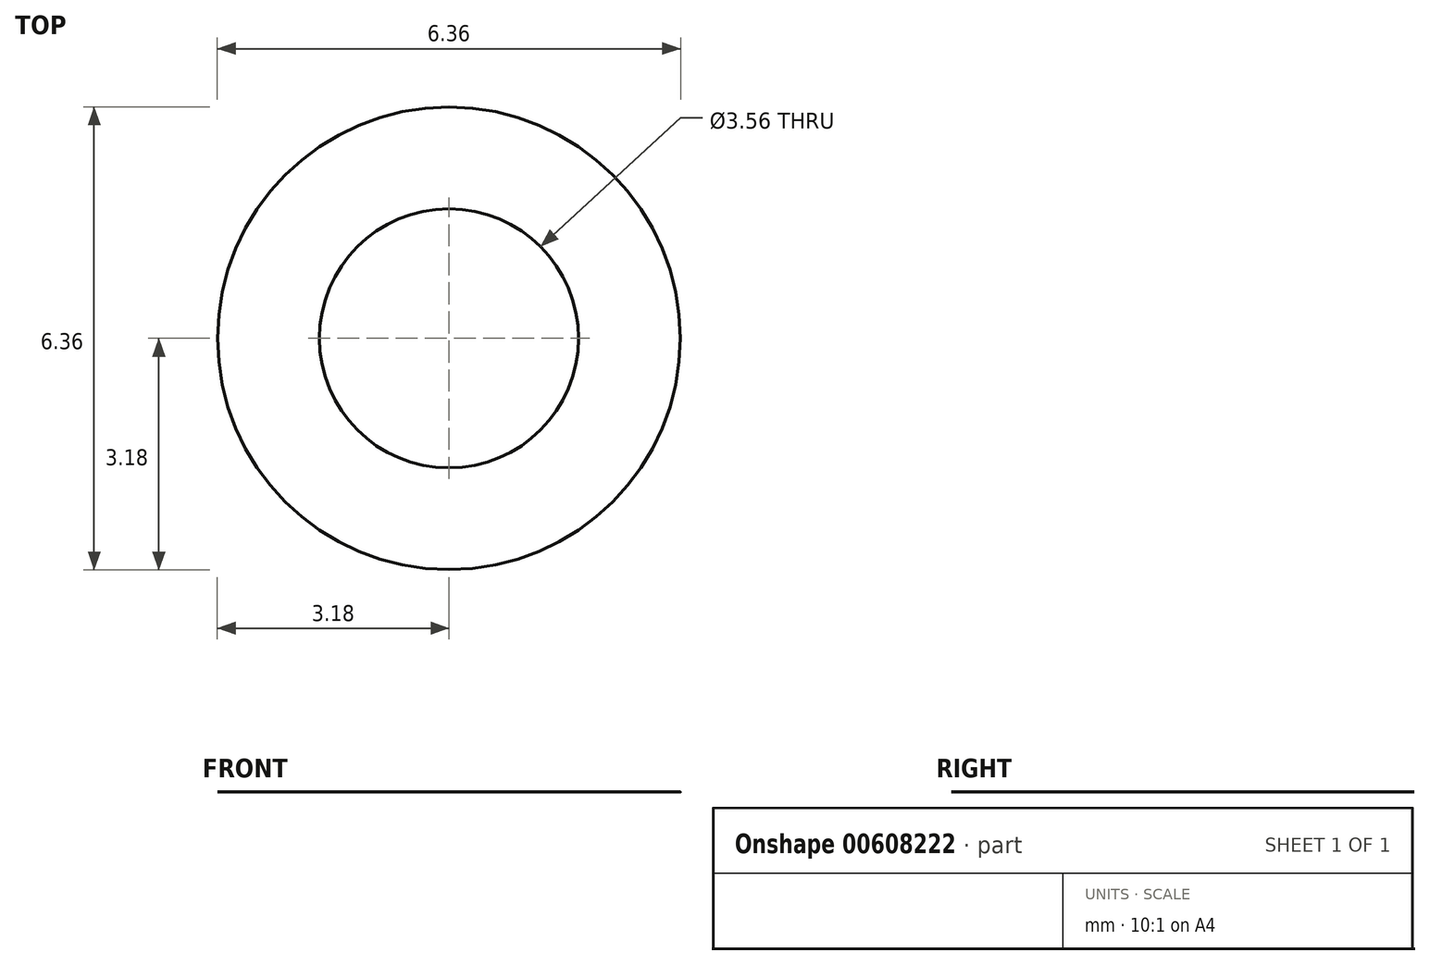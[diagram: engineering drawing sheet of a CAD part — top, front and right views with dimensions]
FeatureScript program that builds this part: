
annotation { "Feature Type Name" : "Feature", "Feature Type Description" : "" }
export const myFeature = defineFeature(function(context is Context, id is Id, definition is map)
    precondition{}
    {
        {
            var Q0;
            Q0=qCreatedBy(makeId("Top.planeOp"),FACE);
            var sketch = newSketch(context, id + "F0", { "sketchPlane" : qUnion([Q0])});
            skCircle(sketch, "E0", {"center": v(0, 0) * mm, "radius": 1.78 * mm});
            skCircle(sketch, "E1", {"center": v(0, 0) * mm, "radius": 3.18 * mm});
            skSolve(sketch);
        }
        {
            var Q0;
            Q0=makeQuery(id+"F0.imprint","IMPRINT",FACE,{"disambiguationData":[TD([[makeQuery(id+"F0.imprint","IMPRINT",EDGE,{"derivedFrom":sQuery(id+"F0.wireOp",EDGE,"E0")}),-1.0]])]});
            extrude(context, id + "F1", {"entities" : qUnion([Q0]), "depth" : 1 / 406.4 * mm, "offsetDistance" : 25 * mm});
        }
    });
